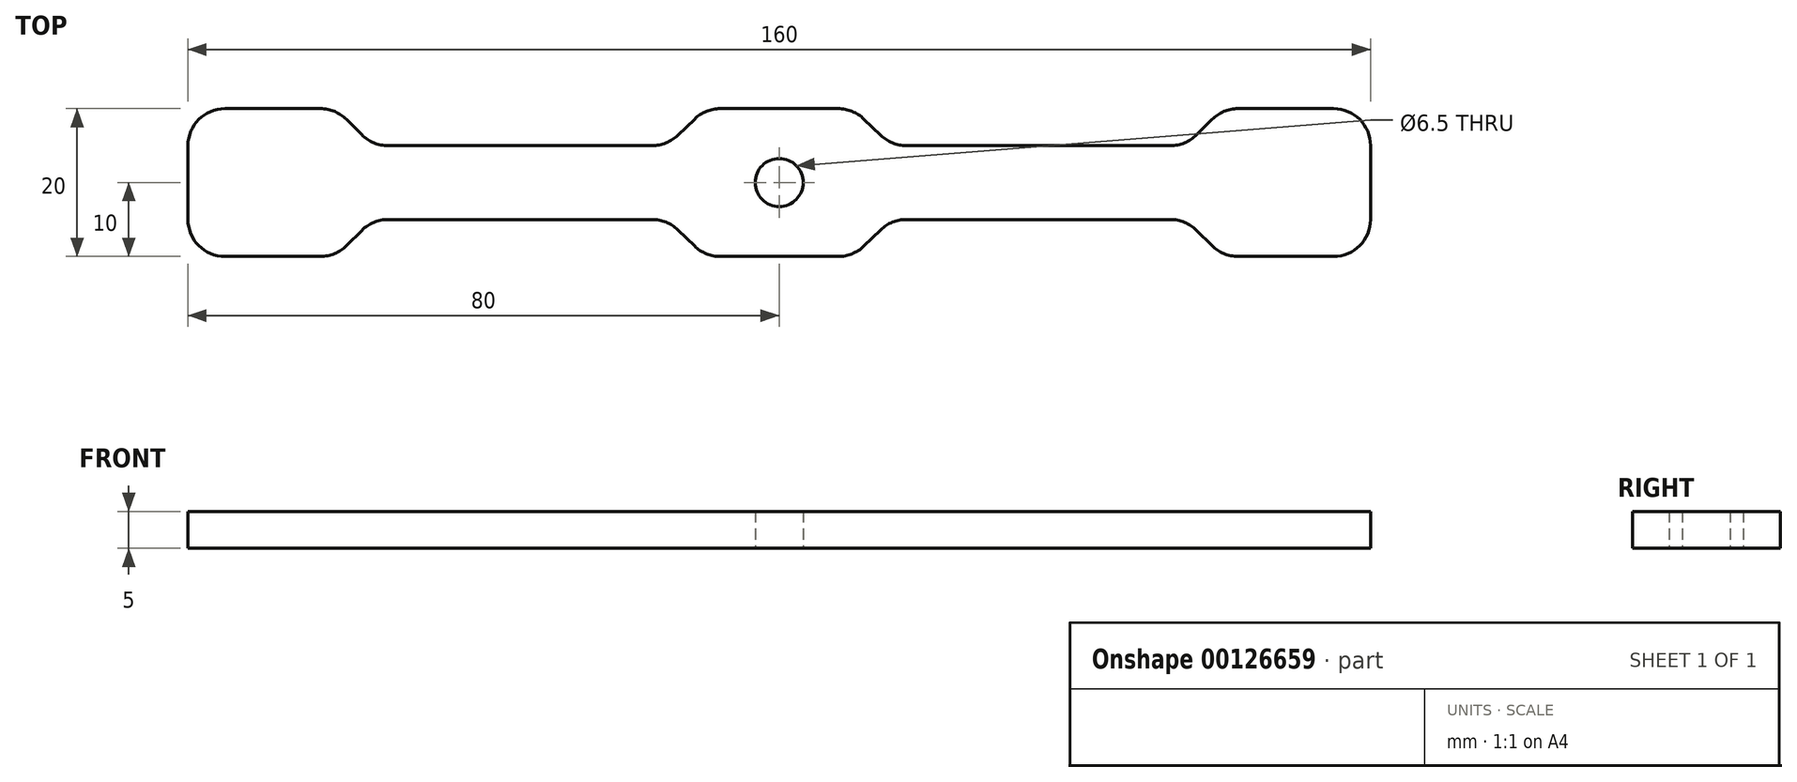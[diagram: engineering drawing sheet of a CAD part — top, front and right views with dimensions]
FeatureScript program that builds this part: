
annotation { "Feature Type Name" : "Feature", "Feature Type Description" : "" }
export const myFeature = defineFeature(function(context is Context, id is Id, definition is map)
    precondition{}
    {
        {
            var Q0;
            Q0=qCreatedBy(makeId("Top.planeOp"),FACE);
            var sketch = newSketch(context, id + "F0", { "sketchPlane" : qUnion([Q0])});
            skLineSegment(sketch, "E0.bottom", {"start": v(-80, -10) * mm, "end": v(80, -10) * mm});
            skLineSegment(sketch, "E0.top", {"start": v(-80, 10) * mm, "end": v(80, 10) * mm});
            skLineSegment(sketch, "E0.left", {"start": v(-80, 10) * mm, "end": v(-80, -10) * mm});
            skLineSegment(sketch, "E0.right", {"start": v(80, 10) * mm, "end": v(80, -10) * mm});
            skLineSegment(sketch, "E1", {"start": v(0, 10) * mm, "end": v(0, -10) * mm, "construction": true});
            skCircle(sketch, "E2", {"center": v(0, 0) * mm, "radius": 3.25 * mm});
            skLineSegment(sketch, "E3", {"start": v(-60, 10) * mm, "end": v(-55, 5) * mm});
            skLineSegment(sketch, "E4", {"start": v(-55, 5) * mm, "end": v(-15.18, 5) * mm});
            skLineSegment(sketch, "E5", {"start": v(-15.18, 5) * mm, "end": v(-10, 10) * mm});
            skLineSegment(sketch, "E6.MirrorCS", {"start": v(-15.18, -5) * mm, "end": v(-10, -10) * mm});
            skLineSegment(sketch, "E7.MirrorCS", {"start": v(-60, -10) * mm, "end": v(-55, -5) * mm});
            skLineSegment(sketch, "E8.MirrorCS", {"start": v(-55, -5) * mm, "end": v(-15.18, -5) * mm});
            skLineSegment(sketch, "E9.MirrorCS", {"start": v(80, -10) * mm, "end": v(-80, -10) * mm});
            skLineSegment(sketch, "E10.MirrorCS", {"start": v(55, -5) * mm, "end": v(15.18, -5) * mm});
            skLineSegment(sketch, "E11.MirrorCS", {"start": v(60, -10) * mm, "end": v(55, -5) * mm});
            skLineSegment(sketch, "E12.MirrorCS", {"start": v(15.18, -5) * mm, "end": v(10, -10) * mm});
            skLineSegment(sketch, "E13.MirrorCS", {"start": v(80, 10) * mm, "end": v(-80, 10) * mm});
            skLineSegment(sketch, "E14.MirrorCS", {"start": v(15.18, 5) * mm, "end": v(10, 10) * mm});
            skLineSegment(sketch, "E15.MirrorCS", {"start": v(55, 5) * mm, "end": v(15.18, 5) * mm});
            skLineSegment(sketch, "E16.MirrorCS", {"start": v(60, 10) * mm, "end": v(55, 5) * mm});
            skSolve(sketch);
        }
        {
            var Q0;
            {var subQ1=sQuery(id+"F0.wireOp",EDGE,"E0.left");Q0=makeQuery(id+"F0.imprint","IMPRINT",FACE,{"disambiguationData":[TD([[makeQuery(id+"F0.imprint","IMPRINT",EDGE,{"derivedFrom":subQ1}),1.0]])]});}
            extrude(context, id + "F1", {"entities" : qUnion([Q0]), "depth" : 5 * mm});
        }
        {
            var Q0;
            Q0=makeQuery(id+"F1.opExtrude","SWEPT_EDGE",EDGE,{"disambiguationData":[OSD([sQuery(id+"F0.wireOp",EDGE,"E0.left"),sQuery(id+"F0.wireOp",EDGE,"E9.MirrorCS")])]});
            var Q1;
            Q1=makeQuery(id+"F1.opExtrude","SWEPT_EDGE",EDGE,{"disambiguationData":[OSD([sQuery(id+"F0.wireOp",EDGE,"E7.MirrorCS"),sQuery(id+"F0.wireOp",EDGE,"E8.MirrorCS")])]});
            var Q2;
            Q2=makeQuery(id+"F1.opExtrude","SWEPT_EDGE",EDGE,{"disambiguationData":[OSD([sQuery(id+"F0.wireOp",EDGE,"E6.MirrorCS"),sQuery(id+"F0.wireOp",EDGE,"E9.MirrorCS")])]});
            var Q3;
            Q3=makeQuery(id+"F1.opExtrude","SWEPT_EDGE",EDGE,{"disambiguationData":[OSD([sQuery(id+"F0.wireOp",EDGE,"E12.MirrorCS"),sQuery(id+"F0.wireOp",EDGE,"E9.MirrorCS")])]});
            var Q4;
            Q4=makeQuery(id+"F1.opExtrude","SWEPT_EDGE",EDGE,{"disambiguationData":[OSD([sQuery(id+"F0.wireOp",EDGE,"E10.MirrorCS"),sQuery(id+"F0.wireOp",EDGE,"E12.MirrorCS")])]});
            var Q5;
            Q5=makeQuery(id+"F1.opExtrude","SWEPT_EDGE",EDGE,{"disambiguationData":[OSD([sQuery(id+"F0.wireOp",EDGE,"E11.MirrorCS"),sQuery(id+"F0.wireOp",EDGE,"E9.MirrorCS")])]});
            var Q6;
            Q6=makeQuery(id+"F1.opExtrude","SWEPT_EDGE",EDGE,{"disambiguationData":[OSD([sQuery(id+"F0.wireOp",EDGE,"E0.right"),sQuery(id+"F0.wireOp",EDGE,"E9.MirrorCS")])]});
            var Q7;
            Q7=makeQuery(id+"F1.opExtrude","SWEPT_EDGE",EDGE,{"disambiguationData":[OSD([sQuery(id+"F0.wireOp",EDGE,"E0.right"),sQuery(id+"F0.wireOp",EDGE,"E13.MirrorCS")])]});
            var Q8;
            Q8=makeQuery(id+"F1.opExtrude","SWEPT_EDGE",EDGE,{"disambiguationData":[OSD([sQuery(id+"F0.wireOp",EDGE,"E13.MirrorCS"),sQuery(id+"F0.wireOp",EDGE,"E16.MirrorCS")])]});
            var Q9;
            Q9=makeQuery(id+"F1.opExtrude","SWEPT_EDGE",EDGE,{"disambiguationData":[OSD([sQuery(id+"F0.wireOp",EDGE,"E13.MirrorCS"),sQuery(id+"F0.wireOp",EDGE,"E14.MirrorCS")])]});
            var Q10;
            Q10=makeQuery(id+"F1.opExtrude","SWEPT_EDGE",EDGE,{"disambiguationData":[OSD([sQuery(id+"F0.wireOp",EDGE,"E14.MirrorCS"),sQuery(id+"F0.wireOp",EDGE,"E15.MirrorCS")])]});
            var Q11;
            Q11=makeQuery(id+"F1.opExtrude","SWEPT_EDGE",EDGE,{"disambiguationData":[OSD([sQuery(id+"F0.wireOp",EDGE,"E3"),sQuery(id+"F0.wireOp",EDGE,"E4")])]});
            var Q12;
            Q12=makeQuery(id+"F1.opExtrude","SWEPT_EDGE",EDGE,{"disambiguationData":[OSD([sQuery(id+"F0.wireOp",EDGE,"E3"),sQuery(id+"F0.wireOp",EDGE,"E13.MirrorCS")])]});
            var Q13;
            Q13=makeQuery(id+"F1.opExtrude","SWEPT_EDGE",EDGE,{"disambiguationData":[OSD([sQuery(id+"F0.wireOp",EDGE,"E0.left"),sQuery(id+"F0.wireOp",EDGE,"E13.MirrorCS")])]});
            var Q14;
            Q14=makeQuery(id+"F1.opExtrude","SWEPT_EDGE",EDGE,{"disambiguationData":[OSD([sQuery(id+"F0.wireOp",EDGE,"E5"),sQuery(id+"F0.wireOp",EDGE,"E13.MirrorCS")])]});
            var Q15;
            Q15=makeQuery(id+"F1.opExtrude","SWEPT_EDGE",EDGE,{"disambiguationData":[OSD([sQuery(id+"F0.wireOp",EDGE,"E15.MirrorCS"),sQuery(id+"F0.wireOp",EDGE,"E16.MirrorCS")])]});
            var Q16;
            Q16=makeQuery(id+"F1.opExtrude","SWEPT_EDGE",EDGE,{"disambiguationData":[OSD([sQuery(id+"F0.wireOp",EDGE,"E4"),sQuery(id+"F0.wireOp",EDGE,"E5")])]});
            var Q17;
            Q17=makeQuery(id+"F1.opExtrude","SWEPT_EDGE",EDGE,{"disambiguationData":[OSD([sQuery(id+"F0.wireOp",EDGE,"E6.MirrorCS"),sQuery(id+"F0.wireOp",EDGE,"E8.MirrorCS")])]});
            var Q18;
            Q18=makeQuery(id+"F1.opExtrude","SWEPT_EDGE",EDGE,{"disambiguationData":[OSD([sQuery(id+"F0.wireOp",EDGE,"E10.MirrorCS"),sQuery(id+"F0.wireOp",EDGE,"E11.MirrorCS")])]});
            var Q19;
            Q19=makeQuery(id+"F1.opExtrude","SWEPT_EDGE",EDGE,{"disambiguationData":[OSD([sQuery(id+"F0.wireOp",EDGE,"E7.MirrorCS"),sQuery(id+"F0.wireOp",EDGE,"E9.MirrorCS")])]});
            fillet(context, id + "F2", {"entities" : qUnion([Q0, Q1, Q2, Q3, Q4, Q5, Q6, Q7, Q8, Q9, Q10, Q11, Q12, Q13, Q14, Q15, Q16, Q17, Q18, Q19]), "radius" : 5 * mm, "tangentPropagation" : true, "allowEdgeOverflow" : false});
        }
    });
